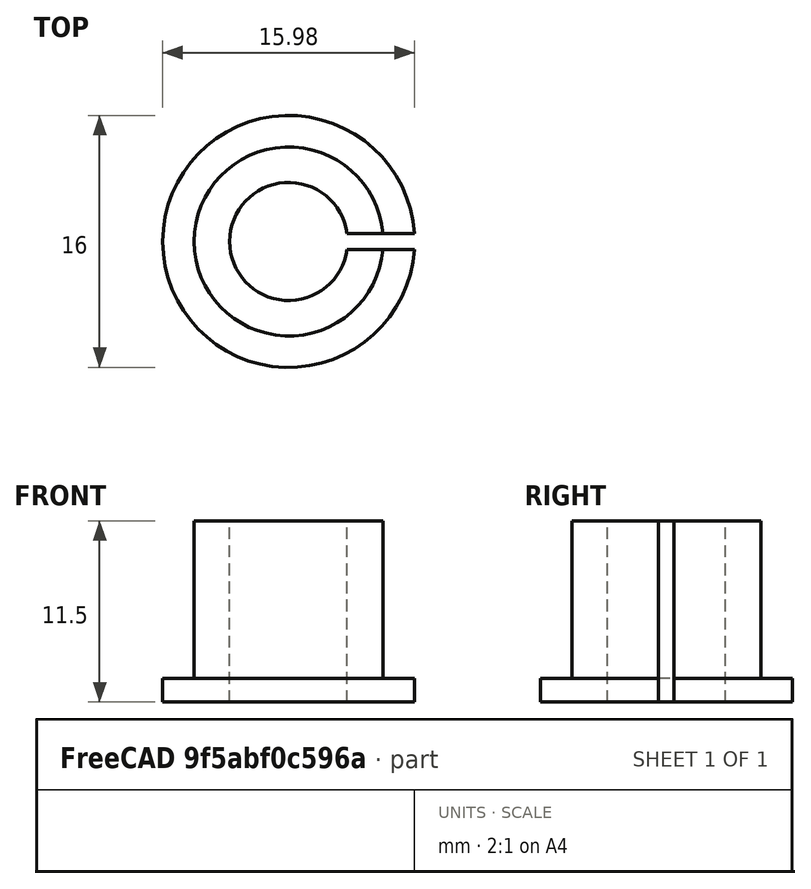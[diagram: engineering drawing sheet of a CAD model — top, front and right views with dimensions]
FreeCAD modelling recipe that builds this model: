
FCSTD DOCUMENT  (FreeCAD 0.17R10423 (Git))
Label: penholder
License: CreativeCommons Attribution-ShareAlike
LicenseURL: http://creativecommons.org/licenses/by-sa/4.0/
objects: Part::Cylinder×3, Part::Cut×2, Part::MultiFuse×1, Part::Box×1
note: 7 computed .brp shape members not serialized (recipe doc carries the construction recipe); baked Part::Feature solids carry a one-line shape summary decoded from their .brp

FEATURE [Part::Cylinder] Cylinder  label="outer"
  Angle = 360
  AttacherType = Attacher::AttachEngine3D
  Height = 11.5
  Radius = 6
FEATURE [Part::Cylinder] Cylinder001  label="base"
  Angle = 360
  AttacherType = Attacher::AttachEngine3D
  Height = 1.5
  Radius = 8
FEATURE [Part::MultiFuse] Fusion
  Shapes = -> [Cylinder,Cylinder001]
FEATURE [Part::Cylinder] Cylinder002  label="inner"
  Angle = 360
  AttacherType = Attacher::AttachEngine3D
  Height = 14
  Placement = pos=(0,0,-1) rot=(0,0,1;0rad)
  Radius = 3.75
FEATURE [Part::Cut] Cut  label="centerhole"
  Base = -> Fusion
  Tool = -> Cylinder002
FEATURE [Part::Box] Box  label="opening"
  AttacherType = Attacher::AttachEngine3D
  Height = 14
  Length = 10
  Placement = pos=(0,-0.5,-1) rot=(0,0,1;0rad)
  Width = 1
FEATURE [Part::Cut] Cut001  label="gap"
  Base = -> Cut
  Tool = -> Box
